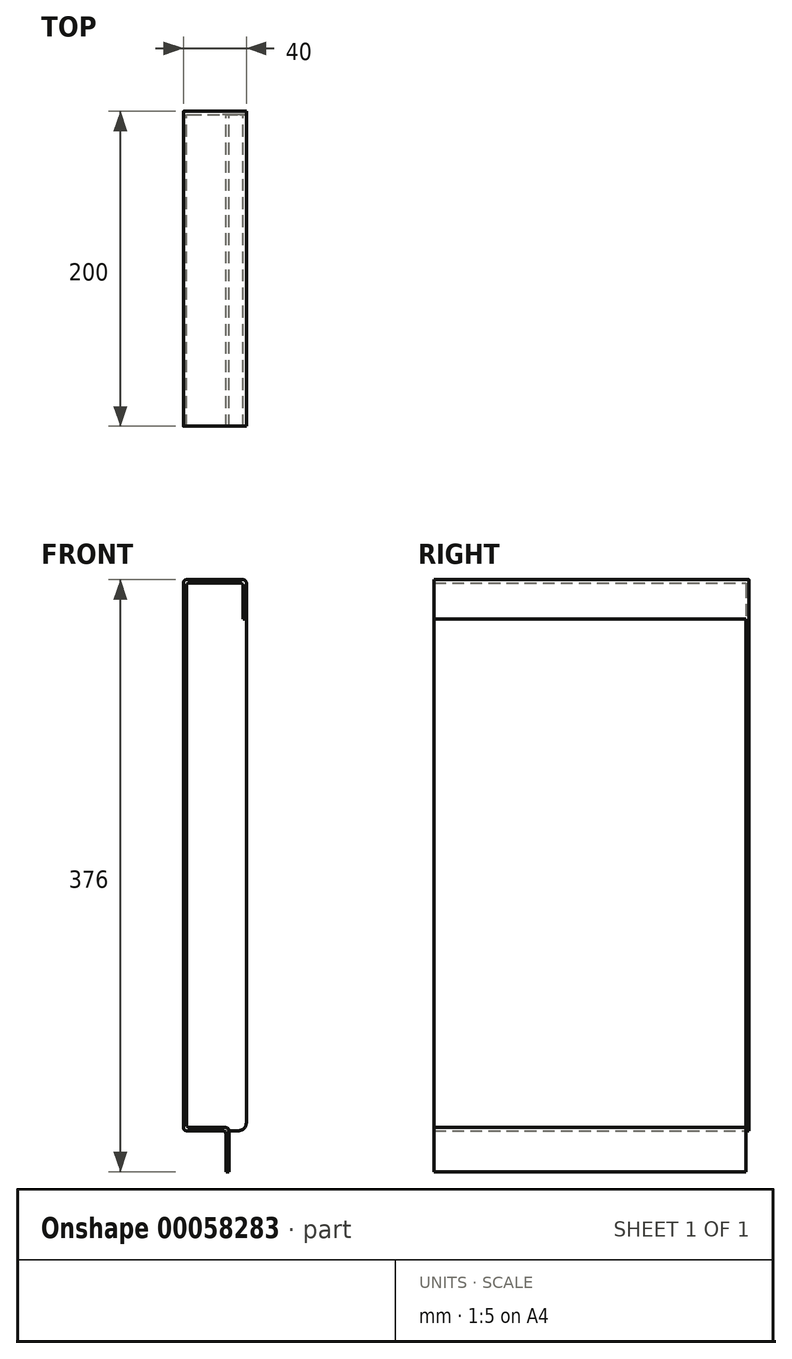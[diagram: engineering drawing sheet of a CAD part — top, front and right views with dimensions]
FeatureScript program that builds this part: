
annotation { "Feature Type Name" : "Feature", "Feature Type Description" : "" }
export const myFeature = defineFeature(function(context is Context, id is Id, definition is map)
    precondition{}
    {
        {
            var Q0;
            Q0=qCreatedBy(makeId("Front.planeOp"),FACE);
            var sketch = newSketch(context, id + "F0", { "sketchPlane" : qUnion([Q0])});
            skLineSegment(sketch, "E0", {"start": v(0, 0) * mm, "end": v(0, -350) * mm});
            skLineSegment(sketch, "E1", {"start": v(0, -350) * mm, "end": v(27, -350) * mm});
            skLineSegment(sketch, "E2", {"start": v(27, -350) * mm, "end": v(27, -376) * mm});
            skLineSegment(sketch, "E3", {"start": v(0, 0) * mm, "end": v(40, 0) * mm});
            skLineSegment(sketch, "E4", {"start": v(40, 0) * mm, "end": v(40, -25) * mm});
            skLineSegment(sketch, "E5.0", {"start": v(38, -2) * mm, "end": v(38, -25) * mm});
            skLineSegment(sketch, "E5.1", {"start": v(29, -348) * mm, "end": v(29, -376) * mm});
            skLineSegment(sketch, "E5.2", {"start": v(2, -348) * mm, "end": v(29, -348) * mm});
            skLineSegment(sketch, "E5.3", {"start": v(2, -2) * mm, "end": v(2, -348) * mm});
            skLineSegment(sketch, "E5.4", {"start": v(2, -2) * mm, "end": v(38, -2) * mm});
            skLineSegment(sketch, "E6", {"start": v(38, -25) * mm, "end": v(40, -25) * mm});
            skLineSegment(sketch, "E7", {"start": v(27, -376) * mm, "end": v(29, -376) * mm});
            skSolve(sketch);
        }
        {
            var Q0;
            Q0=qCreatedBy(makeId("Top.planeOp"),FACE);
            var sketch = newSketch(context, id + "F1", { "sketchPlane" : qUnion([Q0])});
            skLineSegment(sketch, "E8", {"start": v(0, 0) * mm, "end": v(0, 198) * mm});
            skSolve(sketch);
        }
        {
            var Q0;
            Q0=qSketchRegion(id+"F0",true);
            var Q1;
            Q1=qConstructionFilter(qBodyType(qCreatedBy(id+"F1",EDGE),BodyType.WIRE),ConstructionObject.NO);
            sweep(context, id + "F2", {"profiles" : qUnion([Q0]), "path" : qUnion([Q1])});
        }
        {
            var Q0;
            Q0=makeQuery(id+"F2.opSweep","CAP_FACE",FACE,{"disambiguationData":[OSD([sQuery(id+"F0.wireOp",EDGE,"E0"),sQuery(id+"F0.wireOp",EDGE,"E1"),sQuery(id+"F0.wireOp",EDGE,"E2"),sQuery(id+"F0.wireOp",EDGE,"E3"),sQuery(id+"F0.wireOp",EDGE,"E4"),sQuery(id+"F0.wireOp",EDGE,"E5.0"),sQuery(id+"F0.wireOp",EDGE,"E5.1"),sQuery(id+"F0.wireOp",EDGE,"E5.2"),sQuery(id+"F0.wireOp",EDGE,"E5.3"),sQuery(id+"F0.wireOp",EDGE,"E5.4"),sQuery(id+"F0.wireOp",EDGE,"E6"),sQuery(id+"F0.wireOp",EDGE,"E7"),sQuery(id+"F1.wireOp",VERTEX,"E8.end")])],"isStart":false});
            var sketch = newSketch(context, id + "F3", { "sketchPlane" : qUnion([Q0])});
            skLineSegment(sketch, "E9.0", {"start": v(0, -350) * mm, "end": v(0, 0) * mm});
            skLineSegment(sketch, "E10.0", {"start": v(-40, 0) * mm, "end": v(0, 0) * mm});
            skLineSegment(sketch, "E11.0", {"start": v(-40, -25) * mm, "end": v(-40, 0) * mm});
            skLineSegment(sketch, "E12.0", {"start": v(-40, -25) * mm, "end": v(-40, -345) * mm});
            skArc(sketch, "E13.0", {"start": v(-35, -350) * mm, "mid": v(-38.54, -348.54) * mm, "end": v(-40, -345) * mm});
            skLineSegment(sketch, "E14.0", {"start": v(-35, -350) * mm, "end": v(-29, -350) * mm});
            skLineSegment(sketch, "E15.0", {"start": v(-27, -350) * mm, "end": v(0, -350) * mm});
            skLineSegment(sketch, "E16", {"start": v(-29, -350) * mm, "end": v(-27, -350) * mm});
            skSolve(sketch);
        }
        {
            var Q0;
            Q0=qSketchRegion(id+"F3",true);
            extrude(context, id + "F4", {"entities" : qUnion([Q0]), "operationType" : NewBodyOperationType.ADD, "depth" : 2 * mm});
        }
        {
            var Q0;
            Q0=makeQuery(id+"F4.boolean.opBoolean","MERGE",EDGE,{"derivedFrom":[makeQuery(id+"F2.opSweep","SWEPT_EDGE",EDGE,{"disambiguationData":[OSD([sQuery(id+"F0.wireOp",EDGE,"E0"),sQuery(id+"F0.wireOp",EDGE,"E3"),sQuery(id+"F1.wireOp",EDGE,"E8")])]}),makeQuery(id+"F4.opExtrude","SWEPT_EDGE",EDGE,{"disambiguationData":[OSD([sQuery(id+"F3.wireOp",EDGE,"E9.0"),sQuery(id+"F3.wireOp",EDGE,"E10.0")])]})]});
            var Q1;
            Q1=makeQuery(id+"F4.boolean.opBoolean","MERGE",EDGE,{"derivedFrom":[makeQuery(id+"F2.opSweep","SWEPT_EDGE",EDGE,{"disambiguationData":[OSD([sQuery(id+"F0.wireOp",EDGE,"E3"),sQuery(id+"F0.wireOp",EDGE,"E4"),sQuery(id+"F1.wireOp",EDGE,"E8")])]}),makeQuery(id+"F4.opExtrude","SWEPT_EDGE",EDGE,{"disambiguationData":[OSD([sQuery(id+"F3.wireOp",EDGE,"E10.0"),sQuery(id+"F3.wireOp",EDGE,"E11.0")])]})]});
            var Q2;
            Q2=makeQuery(id+"F4.boolean.opBoolean","MERGE",EDGE,{"derivedFrom":[makeQuery(id+"F2.opSweep","SWEPT_EDGE",EDGE,{"disambiguationData":[OSD([sQuery(id+"F0.wireOp",EDGE,"E0"),sQuery(id+"F0.wireOp",EDGE,"E1"),sQuery(id+"F1.wireOp",EDGE,"E8")])]}),makeQuery(id+"F4.opExtrude","SWEPT_EDGE",EDGE,{"disambiguationData":[OSD([sQuery(id+"F3.wireOp",EDGE,"E9.0"),sQuery(id+"F3.wireOp",EDGE,"E15.0")])]})]});
            var Q3;
            Q3=makeQuery(id+"F2.opSweep","SWEPT_EDGE",EDGE,{"disambiguationData":[OSD([sQuery(id+"F0.wireOp",EDGE,"E5.1"),sQuery(id+"F0.wireOp",EDGE,"E5.2"),sQuery(id+"F1.wireOp",EDGE,"E8")])]});
            var Q4;
            Q4=makeQuery(id+"F2.opSweep","SWEPT_EDGE",EDGE,{"disambiguationData":[OSD([sQuery(id+"F0.wireOp",EDGE,"E1"),sQuery(id+"F0.wireOp",EDGE,"E2"),sQuery(id+"F1.wireOp",EDGE,"E8")])]});
            var Q5;
            Q5=makeQuery(id+"F2.opSweep","SWEPT_EDGE",EDGE,{"disambiguationData":[OSD([sQuery(id+"F0.wireOp",EDGE,"E5.2"),sQuery(id+"F0.wireOp",EDGE,"E5.3"),sQuery(id+"F1.wireOp",EDGE,"E8")])]});
            var Q6;
            Q6=makeQuery(id+"F2.opSweep","SWEPT_EDGE",EDGE,{"disambiguationData":[OSD([sQuery(id+"F0.wireOp",EDGE,"E5.3"),sQuery(id+"F0.wireOp",EDGE,"E5.4"),sQuery(id+"F1.wireOp",EDGE,"E8")])]});
            var Q7;
            Q7=makeQuery(id+"F2.opSweep","SWEPT_EDGE",EDGE,{"disambiguationData":[OSD([sQuery(id+"F0.wireOp",EDGE,"E5.0"),sQuery(id+"F0.wireOp",EDGE,"E5.4"),sQuery(id+"F1.wireOp",EDGE,"E8")])]});
            fillet(context, id + "F5", {"entities" : qUnion([Q0, Q1, Q2, Q3, Q4, Q5, Q6, Q7]), "radius" : 2 * mm, "tangentPropagation" : true, "allowEdgeOverflow" : false});
        }
    });
